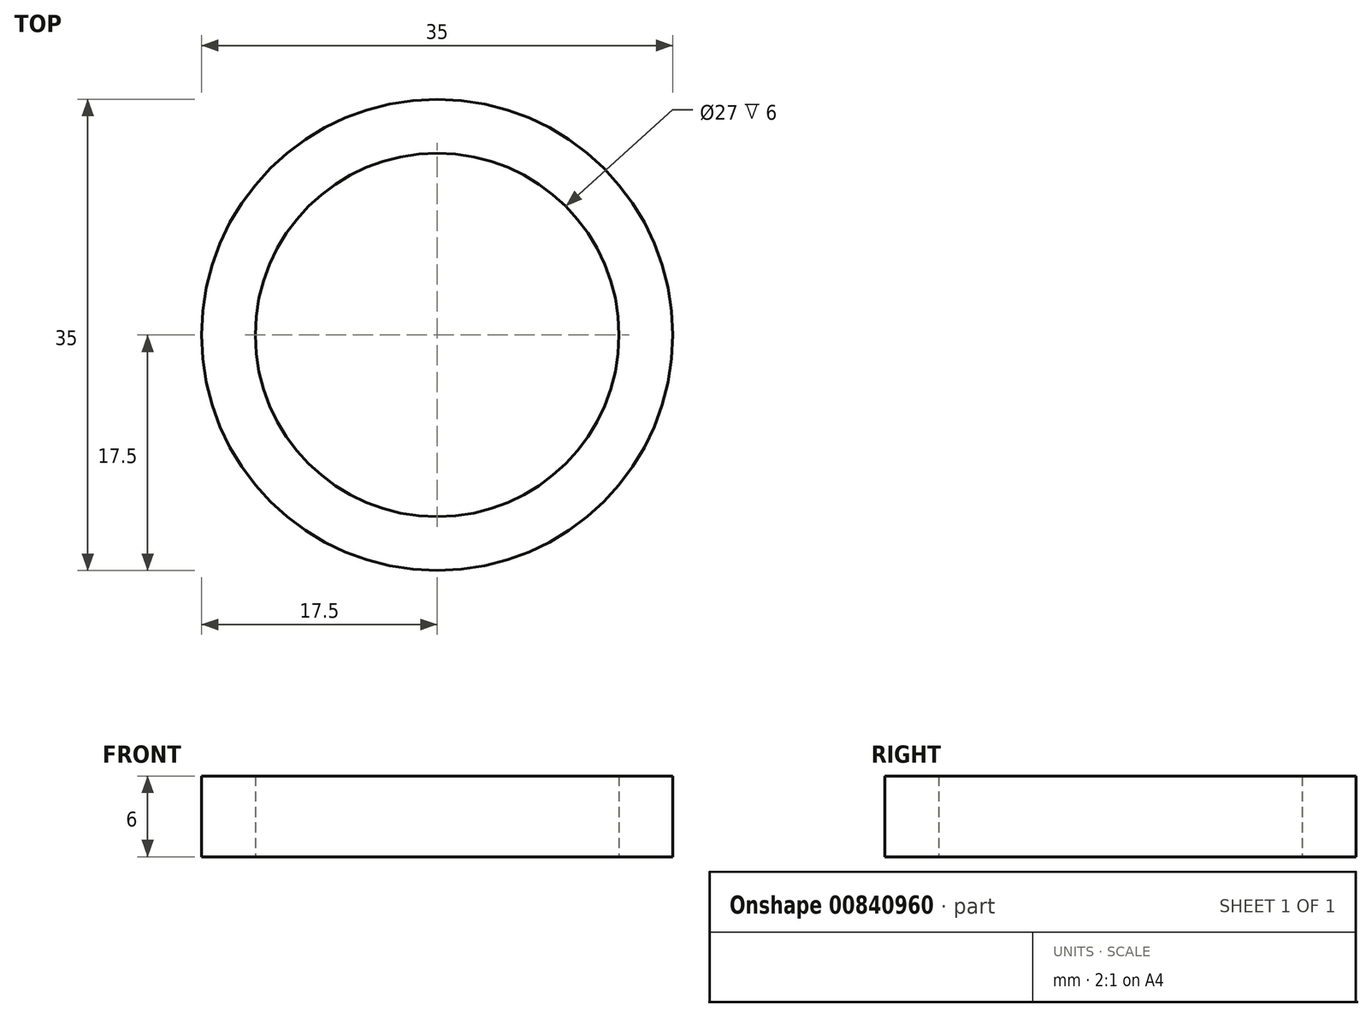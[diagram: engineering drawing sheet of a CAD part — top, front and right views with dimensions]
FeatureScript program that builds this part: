
annotation { "Feature Type Name" : "Feature", "Feature Type Description" : "" }
export const myFeature = defineFeature(function(context is Context, id is Id, definition is map)
    precondition{}
    {
        {
            var Q0;
            Q0=qCreatedBy(makeId("Top.planeOp"),FACE);
            var sketch = newSketch(context, id + "F0", { "sketchPlane" : qUnion([Q0])});
            skCircle(sketch, "E0", {"center": v(0, 0) * mm, "radius": 13.5 * mm});
            skCircle(sketch, "E1", {"center": v(0, 0) * mm, "radius": 17.5 * mm});
            skSolve(sketch);
        }
        {
            var Q0;
            Q0 = qSketchRegion(id + "F0", true);
            extrude(context, id + "F1", {"entities" : qUnion([Q0]), "depth" : 6 * mm, "offsetDistance" : 25 * mm});
        }
    });
